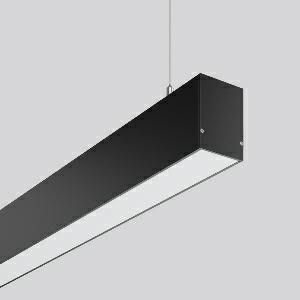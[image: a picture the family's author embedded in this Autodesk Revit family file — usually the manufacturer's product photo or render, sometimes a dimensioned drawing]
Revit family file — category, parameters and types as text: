
# Revit family: less_is_more_50_312318_003_76_e8cc
name_source: partatom
category: Lighting Fixtures
units: mm (PartAtom-declared; Revit-internal decimal feet)

## family parameters
Cut with Voids When Loaded = No
Host = Face
Light Source = No
Part Type = Normal
Room Calculation Point = No
Round Connector Dimension = Use Diameter
Shared = No

## types (1)
- LESS IS MORE 50 (1 x LED Modul 830, 4600 lm, 3000)
    Apparent Load = 40 VA
    CIE Flux Codes = 49 80 96 63 100
    Color Rendering = 80
    Color Temperature = 3000
    Default Elevation = 1800 mm
    Description = Series: LESS IS MORE 50
Linear pendant luminaire for aesthetically sophisticated lighting. Housing: extruded aluminium profile, powder-coated. End cap aluminium powder-coated. Canopy made of aluminium, powder-coated. Diffuser made of non-yellowing plastic (PMMA), opal. Direct 65%, indirect 35% light emission. Suitable for pendant. 2-point steel cable suspension freely positionable and infinitely height-adjustable. Special lengths available on request. LED unit with integrated converter interchangeable and removable. Suitable for through-wiring. With sensors or as a safety luminaire on request. 
Colour: deep black, matt (RAL 9005)
Length: 1127 mm
Width: 57 mm
Height: 75 mm
Suspension length: 2000 mm
Lamp: LED
Socket: without socket
Colour temperature: 3000K
Colour rendering index (CRI): 80
Light source: LED
Socket lamp2: Without base
Colour temperature: 3000K
System power: 40 W
Rated luminous flux: 4600 lm
Luminous efficiency: 115 lm/W
Control gear: Converter, dimmable, DALI
Control gear: Converter, dimmable, DALI
Protection class: I
Type of protection: IP 20
    Height = 75 mm
    Lamp = 1 x LED Modul 830
    Lamp Light Flux = 4600 lm
    Lamp count = 1
    Length = 1127 mm
    Lifetime = 50000 h
    Luminous efficacy = 115 lm/W
    Manufacturer = RZB
    ModVariant = No
    Model = 312318.003.76
    Mounting Place = Ceiling
    Mounting Type = Pendant
    Number of Poles = 1
    OnlyDefault = Yes
    Power Factor = 1
    Product Name = LESS IS MORE 50
    Product group = Pendant LED linear luminaires
    ProductGroupID = 907
    Protection Class = Protection class I
    Protection Degree = IP 20
    RLX_Detail_Level = 1
    RLX_Emergency_Light_Flux = 0 lm
    RLX_Emergency_Type = 0
    RLX_Emergency_Type_DB = No
    RlxData = <blob elided: 39845 chars, md5=277fbdbe>
    Socket = socket
    Standby Power = 0 W
    System Light Flux = 4600 lm
    System Power = 40 W
    Type Comments = Product without accessories
    Type Image = 312318.003.jpg
    URL = http://relux.com
    VarID = ---
    Voltage = 230 V
    Voltage Range = 220-240 V
    Weight = 0.00 kg
    Width = 57 mm

## geometry (parser evidence)
native form markers: Blend x4, Sweep x11
no freeform markers — native parametric forms only
